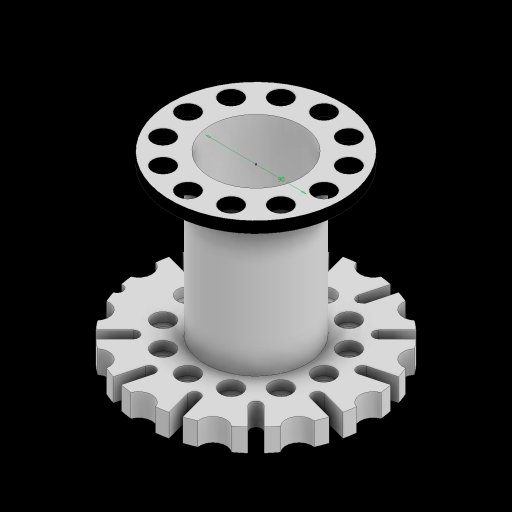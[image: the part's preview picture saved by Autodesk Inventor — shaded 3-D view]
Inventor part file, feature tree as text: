
AUTODESK INVENTOR PART (.ipt)
format: ipt  version: 2023 (Build 270158000, 158)  size: 1,212,928 bytes
history: native  units: mm
features: extrude x7, sketch x7, fillet x1, projected_geometry x1
ambient origin geometry x8: Origin, YZ Plane, XZ Plane, XY Plane, X Axis, Y Axis, Z Axis, Center Point
bodies: Solid1 (feature_tree)
feature tree (16):
  extrude  "Extrusion1"  Depth=150.0mm
  extrude  "Extrusion2"  Depth=120.0mm TaperAngle=360.0deg
  extrude  "Extrusion9"  Depth=10.0mm
  extrude  "Extrusion10"  Depth=10.0mm TaperAngle=360.0deg
  extrude  "Extrusion11"  Depth=18.5mm
  extrude  "Extrusion12"  Depth=10.0mm TaperAngle=0.0deg
  extrude  "Extrusion13"  Depth=140.0mm TaperAngle=0.0deg
  fillet  "Fillet2"  Radius=10.0mm
  sketch  "Sketch1"  dims[d0=150.0mm d1=120.0mm]
  sketch  "Sketch2"  dims[d2=18.5mm d3=120.0mm d5=360.0deg]
  sketch  "Sketch3"  dims[d7=10.0mm d8=0.0mm d9=90.0mm]
  sketch  "Sketch7"  dims[d10=130.0mm d11=0.0mm d67=120.0mm d68=360.0deg d69=10.0mm d70=0.0mm]
  sketch  "Sketch8"  dims[d71=120.0mm d72=18.5mm]
  sketch  "Sketch9"  dims[d73=120.0mm d75=360.0deg d77=10.0mm d78=0.0mm]
  sketch  "Sketch10"  dims[d92=80.0mm d93=140.0mm d94=0.0mm d96=120.0mm d97=200.0mm d98=15.0deg d99=10.0mm d100=10.0mm d101=80.0mm d102=360.0deg d103=6.0mm d104=5.0mm d105=10.0mm d106=0.0mm d107=10.0mm d108=0.0mm d109=2.0mm]
  projected_geometry  "Projected Loop1"
